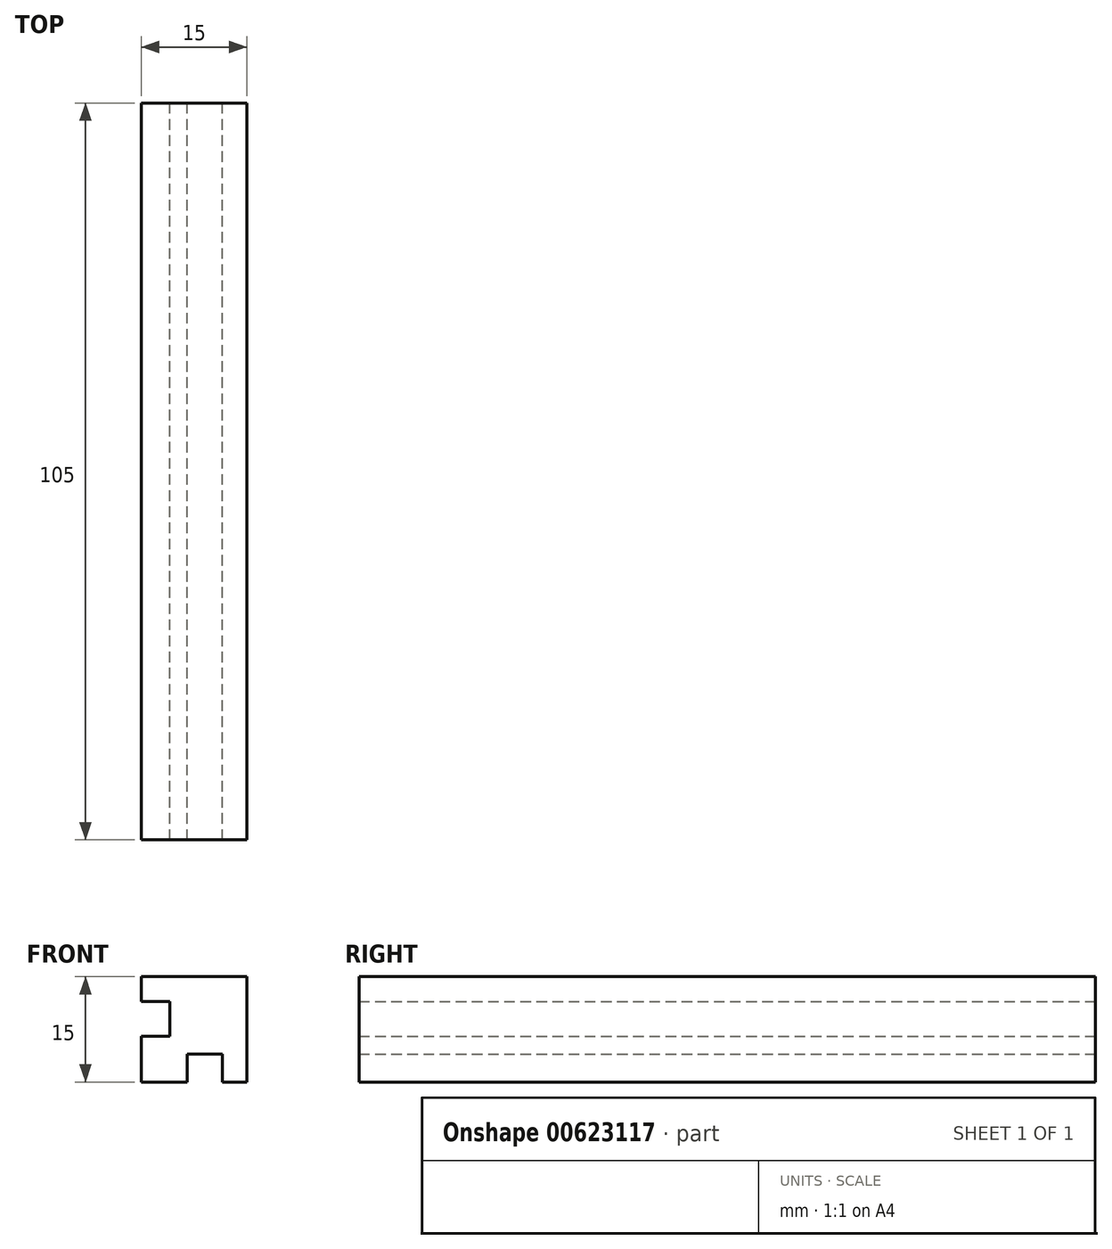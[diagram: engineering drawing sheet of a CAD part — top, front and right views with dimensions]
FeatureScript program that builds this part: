
annotation { "Feature Type Name" : "Feature", "Feature Type Description" : "" }
export const myFeature = defineFeature(function(context is Context, id is Id, definition is map)
    precondition{}
    {
        {
            var Q0;
            Q0=qCreatedBy(makeId("Front.planeOp"),FACE);
            var sketch = newSketch(context, id + "F0", { "sketchPlane" : qUnion([Q0])});
            skLineSegment(sketch, "E0.bottom", {"start": v(0, 0) * mm, "end": v(15, 0) * mm});
            skLineSegment(sketch, "E0.top", {"start": v(0, 15) * mm, "end": v(15, 15) * mm});
            skLineSegment(sketch, "E0.left", {"start": v(0, 0) * mm, "end": v(0, 15) * mm});
            skLineSegment(sketch, "E0.right", {"start": v(15, 0) * mm, "end": v(15, 15) * mm});
            skLineSegment(sketch, "E1.bottom", {"start": v(0, 11.5) * mm, "end": v(4, 11.5) * mm});
            skLineSegment(sketch, "E1.top", {"start": v(0, 6.5) * mm, "end": v(4, 6.5) * mm});
            skLineSegment(sketch, "E1.left", {"start": v(0, 11.5) * mm, "end": v(0, 6.5) * mm});
            skLineSegment(sketch, "E1.right", {"start": v(4, 11.5) * mm, "end": v(4, 6.5) * mm});
            skLineSegment(sketch, "E2.bottom", {"start": v(6.5, 0) * mm, "end": v(11.5, 0) * mm});
            skLineSegment(sketch, "E2.top", {"start": v(6.5, 4) * mm, "end": v(11.5, 4) * mm});
            skLineSegment(sketch, "E2.left", {"start": v(6.5, 0) * mm, "end": v(6.5, 4) * mm});
            skLineSegment(sketch, "E2.right", {"start": v(11.5, 0) * mm, "end": v(11.5, 4) * mm});
            skSolve(sketch);
        }
        {
            var Q0;
            {var subQ4=sQuery(id+"F0.wireOp",EDGE,"E0.top");Q0=makeQuery(id+"F0.imprint","IMPRINT",FACE,{"disambiguationData":[TD([[makeQuery(id+"F0.imprint","IMPRINT",EDGE,{"derivedFrom":subQ4}),-1.0]])]});}
            extrude(context, id + "F1", {"entities" : qUnion([Q0]), "depth" : 105 * mm, "offsetDistance" : 25 * mm});
        }
    });
